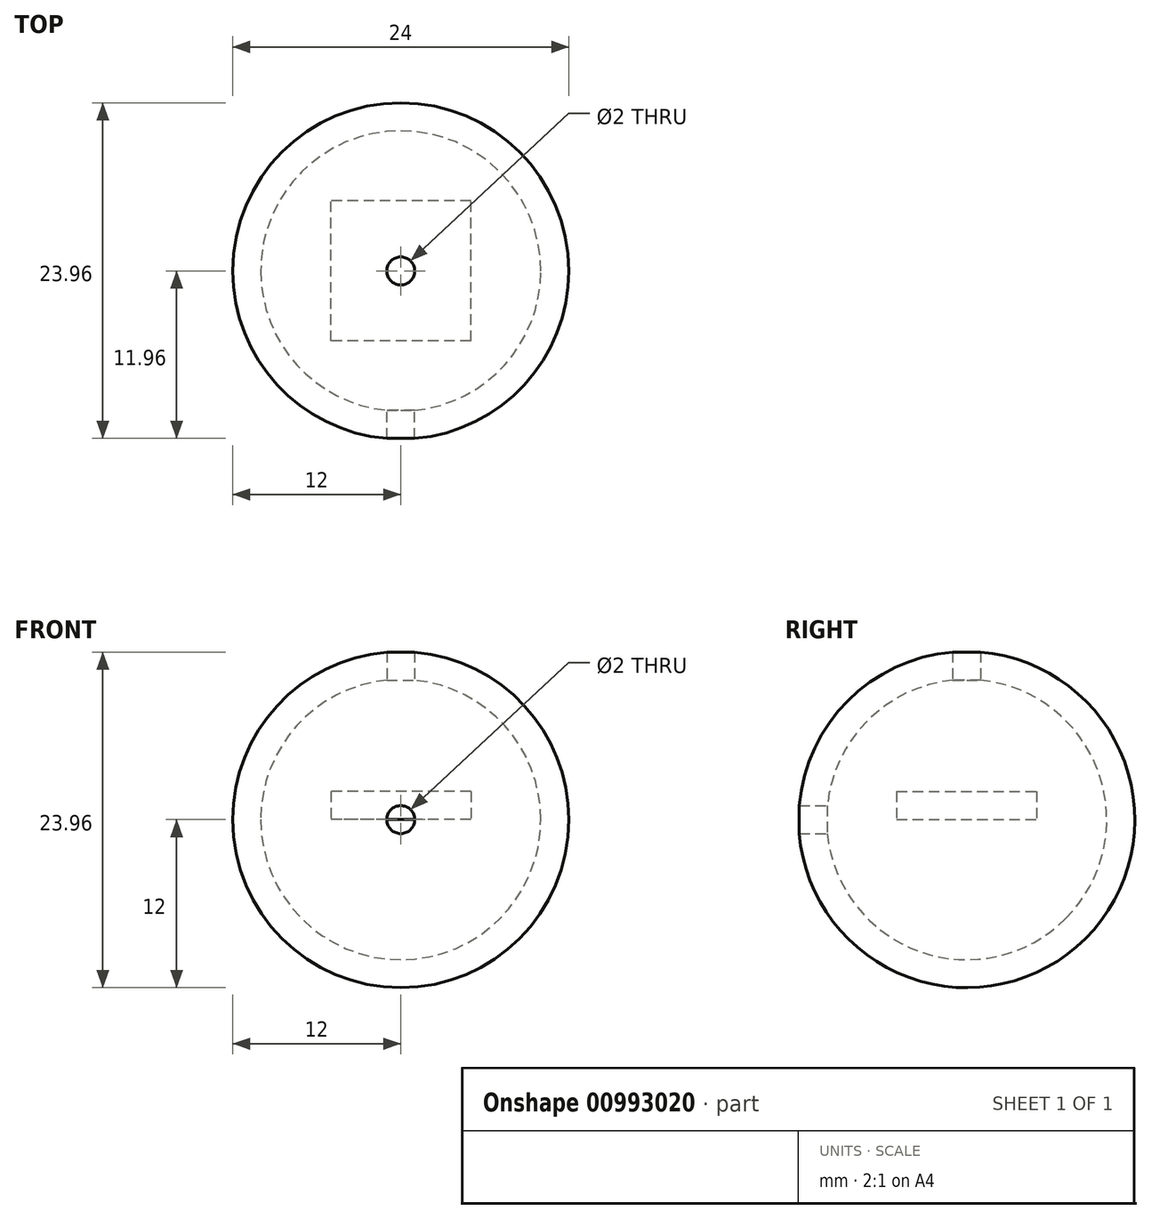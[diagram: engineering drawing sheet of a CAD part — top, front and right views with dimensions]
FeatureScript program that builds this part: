
annotation { "Feature Type Name" : "Feature", "Feature Type Description" : "" }
export const myFeature = defineFeature(function(context is Context, id is Id, definition is map)
    precondition{}
    {
        {
            var Q0;
            Q0=qCreatedBy(makeId("Top.planeOp"),FACE);
            var sketch = newSketch(context, id + "F0", { "sketchPlane" : qUnion([Q0])});
            skArc(sketch, "E0", {"start": v(10, 0) * mm, "mid": v(0, 10) * mm, "end": v(-10, 0) * mm});
            skArc(sketch, "E1", {"start": v(12, 0) * mm, "mid": v(0, 12) * mm, "end": v(-12, 0) * mm});
            skLineSegment(sketch, "E2", {"start": v(-12, 0) * mm, "end": v(-10, 0) * mm});
            skLineSegment(sketch, "E3.trimOffspring", {"start": v(10, 0) * mm, "end": v(12, 0) * mm});
            skSolve(sketch);
        }
        {
            var Q0;
            Q0=qCreatedBy(makeId("Top.planeOp"),FACE);
            var sketch = newSketch(context, id + "F1", { "sketchPlane" : qUnion([Q0])});
            skLineSegment(sketch, "E4", {"start": v(0, 0) * mm, "end": v(69.02, 0) * mm});
            skSolve(sketch);
        }
        {
            var Q0;
            Q0=makeQuery(id+"F0.imprint","IMPRINT",FACE,{"disambiguationData":[TD([[makeQuery(id+"F0.imprint","IMPRINT",EDGE,{"derivedFrom":sQuery(id+"F0.wireOp",EDGE,"E0")}),-1.0]])]});
            var Q1;
            Q1=sQuery(id+"F1.wireOp",EDGE,"E4");
            revolve(context, id + "F2", {"surfaceOperationType" : NewSurfaceOperationType.NEW, "entities" : qUnion([Q0]), "axis" : qUnion([Q1]), "revolveType" : RevolveType.FULL});
        }
        {
            var Q0;
            Q0=qCreatedBy(makeId("Top.planeOp"),FACE);
            var sketch = newSketch(context, id + "F3", { "sketchPlane" : qUnion([Q0])});
            skCircle(sketch, "E5", {"center": v(0, 0) * mm, "radius": 1 * mm});
            skSolve(sketch);
        }
        {
            var Q0;
            Q0=makeQuery(id+"F3.imprint","IMPRINT",FACE,{"disambiguationData":[TD([[makeQuery(id+"F3.imprint","IMPRINT",EDGE,{"derivedFrom":sQuery(id+"F3.wireOp",EDGE,"E5")}),1.0]])]});
            extrude(context, id + "F4", {"entities" : qUnion([Q0]), "depth" : 200 * mm, "offsetDistance" : 25 * mm});
        }
        {
            var Q0;
            Q0=makeQuery(id+"F4.opExtrude","SWEPT_BODY",BODY,{"disambiguationData":[OSD([sQuery(id+"F3.wireOp",EDGE,"E5")])]});
            var Q1;
            Q1=makeQuery(id+"F2.opRevolve","SWEPT_BODY",BODY,{"disambiguationData":[OSD([sQuery(id+"F0.wireOp",EDGE,"E0"),sQuery(id+"F0.wireOp",EDGE,"E1"),sQuery(id+"F0.wireOp",EDGE,"E2"),sQuery(id+"F0.wireOp",EDGE,"E3.trimOffspring")])]});
            booleanBodies(context, id + "F5", {"operationType" : BooleanOperationType.SUBTRACTION, "tools" : qUnion([Q0]), "targets" : qUnion([Q1])});
        }
        {
            var Q0;
            Q0=qCreatedBy(makeId("Front.planeOp"),FACE);
            var sketch = newSketch(context, id + "F6", { "sketchPlane" : qUnion([Q0])});
            skCircle(sketch, "E6", {"center": v(0, 0) * mm, "radius": 1 * mm});
            skSolve(sketch);
        }
        {
            var Q0;
            Q0=makeQuery(id+"F6.imprint","IMPRINT",FACE,{"disambiguationData":[TD([[makeQuery(id+"F6.imprint","IMPRINT",EDGE,{"derivedFrom":sQuery(id+"F6.wireOp",EDGE,"E6")}),1.0]])]});
            var Q1;
            Q1=sQuery(id+"F6.wireOp",EDGE,"E6");
            extrude(context, id + "F7", {"entities" : qUnion([Q0]), "surfaceEntities" : qUnion([Q1]), "depth" : 25 * mm, "offsetDistance" : 25 * mm});
        }
        {
            var Q0;
            Q0=makeQuery(id+"F7.opExtrude","SWEPT_BODY",BODY,{"disambiguationData":[OSD([sQuery(id+"F6.wireOp",EDGE,"E6")])]});
            var Q1;
            Q1=makeQuery(id+"F2.opRevolve","SWEPT_BODY",BODY,{"disambiguationData":[OSD([sQuery(id+"F0.wireOp",EDGE,"E0"),sQuery(id+"F0.wireOp",EDGE,"E1"),sQuery(id+"F0.wireOp",EDGE,"E2"),sQuery(id+"F0.wireOp",EDGE,"E3.trimOffspring")])]});
            booleanBodies(context, id + "F8", {"operationType" : BooleanOperationType.SUBTRACTION, "tools" : qUnion([Q0]), "targets" : qUnion([Q1])});
        }
        {
            var Q0;
            Q0=qCreatedBy(makeId("Top.planeOp"),FACE);
            var sketch = newSketch(context, id + "F9", { "sketchPlane" : qUnion([Q0])});
            skLineSegment(sketch, "E7.bottom", {"start": v(5, -5) * mm, "end": v(-5, -5) * mm});
            skLineSegment(sketch, "E7.top", {"start": v(5, 5) * mm, "end": v(-5, 5) * mm});
            skLineSegment(sketch, "E7.left", {"start": v(5, -5) * mm, "end": v(5, 5) * mm});
            skLineSegment(sketch, "E7.right", {"start": v(-5, -5) * mm, "end": v(-5, 5) * mm});
            skPoint(sketch, "E7.middle", {"position": v(0, 0) * mm});
            skSolve(sketch);
        }
        {
            var Q0;
            Q0=makeQuery(id+"F9.imprint","IMPRINT",FACE,{"disambiguationData":[TD([[makeQuery(id+"F9.imprint","IMPRINT",EDGE,{"derivedFrom":sQuery(id+"F9.wireOp",EDGE,"E7.bottom")}),-1.0]])]});
            extrude(context, id + "F10", {"entities" : qUnion([Q0]), "depth" : 2 * mm, "offsetDistance" : 25 * mm});
        }
    });
